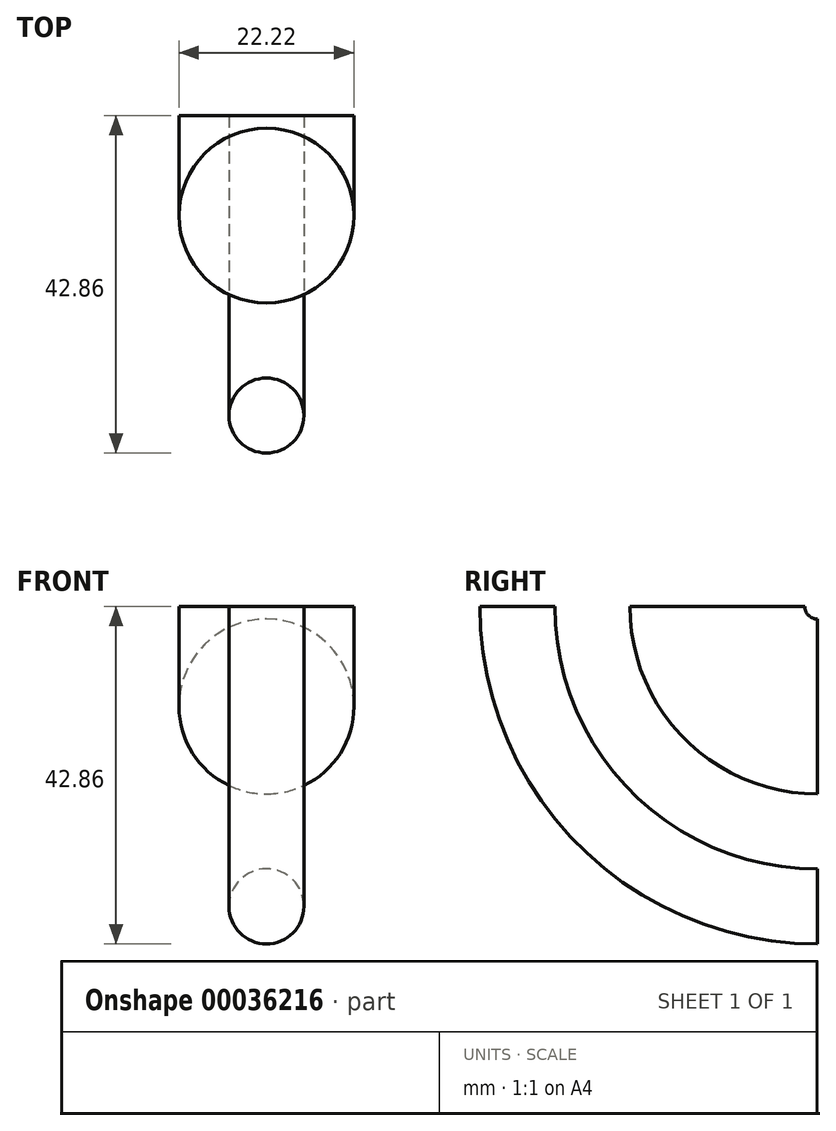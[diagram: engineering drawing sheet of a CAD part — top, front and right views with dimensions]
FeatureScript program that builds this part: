
annotation { "Feature Type Name" : "Feature", "Feature Type Description" : "" }
export const myFeature = defineFeature(function(context is Context, id is Id, definition is map)
    precondition{}
    {
        {
            var Q0;
            Q0=qCreatedBy(makeId("Front.planeOp"),FACE);
            var sketch = newSketch(context, id + "F0", { "sketchPlane" : qUnion([Q0])});
            skCircle(sketch, "E0", {"center": v(0, 0) * mm, "radius": 4.76 * mm});
            skCircle(sketch, "E1", {"center": v(0, 25.4) * mm, "radius": 11.11 * mm});
            skSolve(sketch);
        }
        {
            var Q0;
            Q0=qCreatedBy(makeId("Right.planeOp"),FACE);
            var sketch = newSketch(context, id + "F1", { "sketchPlane" : qUnion([Q0])});
            skArc(sketch, "E2", {"start": v(-38.1, 38.1) * mm, "mid": v(-26.94, 11.16) * mm, "end": v(0, 0) * mm});
            skSolve(sketch);
        }
        {
            var Q0;
            Q0=makeQuery(id+"F0.imprint","IMPRINT",FACE,{"disambiguationData":[TD([[makeQuery(id+"F0.imprint","IMPRINT",EDGE,{"derivedFrom":sQuery(id+"F0.wireOp",EDGE,"E1")}),1.0]])]});
            var Q1;
            Q1=makeQuery(id+"F0.imprint","IMPRINT",FACE,{"disambiguationData":[TD([[makeQuery(id+"F0.imprint","IMPRINT",EDGE,{"derivedFrom":sQuery(id+"F0.wireOp",EDGE,"E0")}),1.0]])]});
            var Q2;
            Q2=sQuery(id+"F1.wireOp",EDGE,"E2");
            sweep(context, id + "F2", {"profiles" : qUnion([Q0, Q1]), "path" : qUnion([Q2])});
        }
    });
